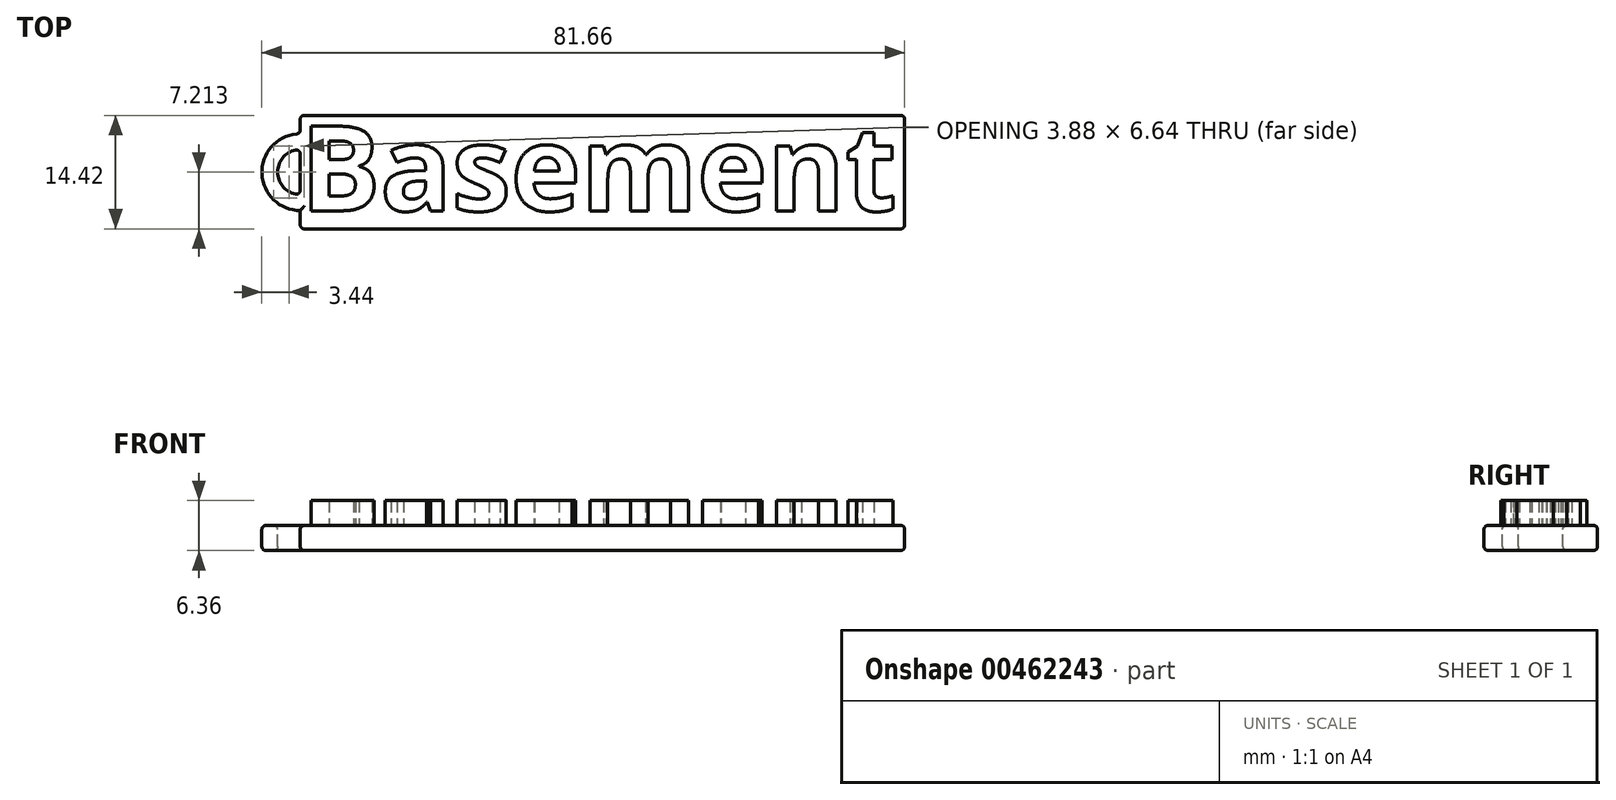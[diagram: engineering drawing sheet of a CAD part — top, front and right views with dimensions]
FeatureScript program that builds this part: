
annotation { "Feature Type Name" : "Feature", "Feature Type Description" : "" }
export const myFeature = defineFeature(function(context is Context, id is Id, definition is map)
    precondition{}
    {
        {
            var Q0;
            Q0=qCreatedBy(makeId("Top.planeOp"),FACE);
            var sketch = newSketch(context, id + "F0", { "sketchPlane" : qUnion([Q0])});
            skText(sketch, "E0", { "text": "Basement", "fontName": "OpenSans-Bold.ttf"});
            const initialGuessF0  = {"E0": [-0.0381, -0.00497, 1, 0, 0.01084]};
            skSetInitialGuess(sketch, initialGuessF0);
            skSolve(sketch);
        }
        {
            var Q0;
            Q0 = qSketchRegion(id + "F0", true);
            extrude(context, id + "F1", {"entities" : qUnion([Q0]), "depth" : 3.17 * mm});
        }
        {
            var Q0;
            Q0=qCreatedBy(makeId("Top.planeOp"),FACE);
            var sketch = newSketch(context, id + "F2", { "sketchPlane" : qUnion([Q0])});
            skLineSegment(sketch, "E1.bottom", {"start": v(-37.67, 7.15) * mm, "end": v(38.14, 7.15) * mm});
            skLineSegment(sketch, "E1.top", {"start": v(-37.67, -7.27) * mm, "end": v(38.14, -7.27) * mm});
            skLineSegment(sketch, "E1.left", {"start": v(-38.16, 6.67) * mm, "end": v(-38.16, 4.82) * mm});
            skLineSegment(sketch, "E1.right", {"start": v(38.63, 6.67) * mm, "end": v(38.63, -6.78) * mm});
            skArc(sketch, "E2", {"start": v(-38.16, 4.82) * mm, "mid": v(-43.03, -0.06) * mm, "end": v(-38.16, -4.93) * mm});
            skArc(sketch, "E3", {"start": v(-38.16, 2.81) * mm, "mid": v(-41.02, -0.06) * mm, "end": v(-38.16, -2.93) * mm});
            skLineSegment(sketch, "E4.trimOffspring", {"start": v(-38.16, 2.81) * mm, "end": v(-38.16, -2.93) * mm});
            skLineSegment(sketch, "E5.trimOffspring", {"start": v(-38.16, -4.93) * mm, "end": v(-38.16, -6.78) * mm});
            skPoint(sketch, "E6.visualSharp", {"position": v(-38.16, 7.15) * mm});
            skPoint(sketch, "E7.visualSharp", {"position": v(-38.16, -7.27) * mm});
            skPoint(sketch, "E8.visualSharp", {"position": v(38.63, 7.15) * mm});
            skPoint(sketch, "E9.visualSharp", {"position": v(38.63, -7.27) * mm});
            skLineSegment(sketch, "E10", {"start": v(-38.16, 6.67) * mm, "end": v(-38.16, 7.15) * mm});
            skLineSegment(sketch, "E11", {"start": v(-37.67, 7.15) * mm, "end": v(-38.16, 7.15) * mm});
            skLineSegment(sketch, "E12", {"start": v(-38.16, -6.78) * mm, "end": v(-38.16, -7.27) * mm});
            skLineSegment(sketch, "E13", {"start": v(-37.67, -7.27) * mm, "end": v(-38.16, -7.27) * mm});
            skLineSegment(sketch, "E14", {"start": v(38.14, 7.15) * mm, "end": v(38.63, 7.15) * mm});
            skLineSegment(sketch, "E15", {"start": v(38.63, 6.67) * mm, "end": v(38.63, 7.15) * mm});
            skLineSegment(sketch, "E16", {"start": v(38.14, -7.27) * mm, "end": v(38.63, -7.27) * mm});
            skLineSegment(sketch, "E17", {"start": v(38.63, -6.78) * mm, "end": v(38.63, -7.27) * mm});
            skSolve(sketch);
        }
        {
            var Q0;
            Q0 = qSketchRegion(id + "F2", true);
            extrude(context, id + "F3", {"entities" : qUnion([Q0]), "operationType" : NewBodyOperationType.ADD, "oppositeDirection" : true, "depth" : 3.17 * mm});
        }
        {
            var Q0;
            Q0=makeQuery(id+"F3.opExtrude","CAP_EDGE",EDGE,{"disambiguationData":[OSD([sQuery(id+"F2.wireOp",EDGE,"E1.bottom"),sQuery(id+"F2.wireOp",EDGE,"E11"),sQuery(id+"F2.wireOp",EDGE,"E14")])],"isStart":true});
            var Q1;
            Q1=makeQuery(id+"F3.opExtrude","CAP_EDGE",EDGE,{"disambiguationData":[OSD([sQuery(id+"F2.wireOp",EDGE,"E1.bottom"),sQuery(id+"F2.wireOp",EDGE,"E11"),sQuery(id+"F2.wireOp",EDGE,"E14")])],"isStart":false});
            var Q2;
            Q2=makeQuery(id+"F3.opExtrude","SWEPT_EDGE",EDGE,{"disambiguationData":[OSD([sQuery(id+"F2.wireOp",EDGE,"E10"),sQuery(id+"F2.wireOp",EDGE,"E11")])]});
            var Q3;
            Q3=makeQuery(id+"F3.opExtrude","SWEPT_EDGE",EDGE,{"disambiguationData":[OSD([sQuery(id+"F2.wireOp",EDGE,"E1.left"),sQuery(id+"F2.wireOp",EDGE,"E2")])]});
            var Q4;
            Q4=makeQuery(id+"F3.opExtrude","CAP_EDGE",EDGE,{"disambiguationData":[OSD([sQuery(id+"F2.wireOp",EDGE,"E1.left"),sQuery(id+"F2.wireOp",EDGE,"E10")])],"isStart":true});
            var Q5;
            Q5=makeQuery(id+"F3.opExtrude","CAP_EDGE",EDGE,{"disambiguationData":[OSD([sQuery(id+"F2.wireOp",EDGE,"E2")])],"isStart":true});
            var Q6;
            Q6=makeQuery(id+"F3.opExtrude","CAP_EDGE",EDGE,{"disambiguationData":[OSD([sQuery(id+"F2.wireOp",EDGE,"E5.trimOffspring"),sQuery(id+"F2.wireOp",EDGE,"E12")])],"isStart":true});
            var Q7;
            Q7=makeQuery(id+"F3.opExtrude","CAP_EDGE",EDGE,{"disambiguationData":[OSD([sQuery(id+"F2.wireOp",EDGE,"E1.top"),sQuery(id+"F2.wireOp",EDGE,"E13"),sQuery(id+"F2.wireOp",EDGE,"E16")])],"isStart":true});
            var Q8;
            Q8=makeQuery(id+"F3.opExtrude","CAP_EDGE",EDGE,{"disambiguationData":[OSD([sQuery(id+"F2.wireOp",EDGE,"E1.right"),sQuery(id+"F2.wireOp",EDGE,"E15"),sQuery(id+"F2.wireOp",EDGE,"E17")])],"isStart":true});
            var Q9;
            Q9=makeQuery(id+"F3.opExtrude","SWEPT_EDGE",EDGE,{"disambiguationData":[OSD([sQuery(id+"F2.wireOp",EDGE,"E14"),sQuery(id+"F2.wireOp",EDGE,"E15")])]});
            var Q10;
            Q10=makeQuery(id+"F3.opExtrude","SWEPT_EDGE",EDGE,{"disambiguationData":[OSD([sQuery(id+"F2.wireOp",EDGE,"E16"),sQuery(id+"F2.wireOp",EDGE,"E17")])]});
            var Q11;
            Q11=makeQuery(id+"F3.opExtrude","CAP_EDGE",EDGE,{"disambiguationData":[OSD([sQuery(id+"F2.wireOp",EDGE,"E1.top"),sQuery(id+"F2.wireOp",EDGE,"E13"),sQuery(id+"F2.wireOp",EDGE,"E16")])],"isStart":false});
            var Q12;
            Q12=makeQuery(id+"F3.opExtrude","CAP_EDGE",EDGE,{"disambiguationData":[OSD([sQuery(id+"F2.wireOp",EDGE,"E1.right"),sQuery(id+"F2.wireOp",EDGE,"E15"),sQuery(id+"F2.wireOp",EDGE,"E17")])],"isStart":false});
            var Q13;
            Q13=makeQuery(id+"F3.opExtrude","CAP_EDGE",EDGE,{"disambiguationData":[OSD([sQuery(id+"F2.wireOp",EDGE,"E1.left"),sQuery(id+"F2.wireOp",EDGE,"E10")])],"isStart":false});
            var Q14;
            Q14=makeQuery(id+"F3.opExtrude","CAP_EDGE",EDGE,{"disambiguationData":[OSD([sQuery(id+"F2.wireOp",EDGE,"E2")])],"isStart":false});
            var Q15;
            Q15=makeQuery(id+"F3.opExtrude","CAP_EDGE",EDGE,{"disambiguationData":[OSD([sQuery(id+"F2.wireOp",EDGE,"E5.trimOffspring"),sQuery(id+"F2.wireOp",EDGE,"E12")])],"isStart":false});
            var Q16;
            Q16=makeQuery(id+"F3.opExtrude","SWEPT_EDGE",EDGE,{"disambiguationData":[OSD([sQuery(id+"F2.wireOp",EDGE,"E12"),sQuery(id+"F2.wireOp",EDGE,"E13")])]});
            var Q17;
            Q17=makeQuery(id+"F3.opExtrude","CAP_EDGE",EDGE,{"disambiguationData":[OSD([sQuery(id+"F2.wireOp",EDGE,"E4.trimOffspring")])],"isStart":false});
            var Q18;
            Q18=makeQuery(id+"F3.opExtrude","CAP_EDGE",EDGE,{"disambiguationData":[OSD([sQuery(id+"F2.wireOp",EDGE,"E3")])],"isStart":false});
            var Q19;
            Q19=makeQuery(id+"F3.opExtrude","CAP_EDGE",EDGE,{"disambiguationData":[OSD([sQuery(id+"F2.wireOp",EDGE,"E4.trimOffspring")])],"isStart":true});
            var Q20;
            Q20=makeQuery(id+"F3.opExtrude","CAP_EDGE",EDGE,{"disambiguationData":[OSD([sQuery(id+"F2.wireOp",EDGE,"E3")])],"isStart":true});
            var Q21;
            {var subQ0=sQuery(id+"F2.wireOp",EDGE,"E4.trimOffspring");var subQ1=sQuery(id+"F2.wireOp",EDGE,"E3");Q21=makeQuery(id+"F3.opExtrude","SWEPT_EDGE",EDGE,{"disambiguationData":[OSD([subQ1,subQ0]),TDD([makeQuery(id+"F2.imprint","INTERSECT",VERTEX,{"disambiguationData":[OD(0.0)],"derivedFrom":[subQ1,subQ0]})])]});}
            var Q22;
            {var subQ0=sQuery(id+"F2.wireOp",EDGE,"E4.trimOffspring");var subQ1=sQuery(id+"F2.wireOp",EDGE,"E3");Q22=makeQuery(id+"F3.opExtrude","SWEPT_EDGE",EDGE,{"disambiguationData":[OSD([subQ1,subQ0]),TDD([makeQuery(id+"F2.imprint","INTERSECT",VERTEX,{"disambiguationData":[OD(1.0)],"derivedFrom":[subQ1,subQ0]})])]});}
            fillet(context, id + "F4", {"entities" : qUnion([Q0, Q1, Q2, Q3, Q4, Q5, Q6, Q7, Q8, Q9, Q10, Q11, Q12, Q13, Q14, Q15, Q16, Q17, Q18, Q19, Q20, Q21, Q22]), "radius" : 0.5 * mm, "tangentPropagation" : true, "allowEdgeOverflow" : false});
        }
    });
